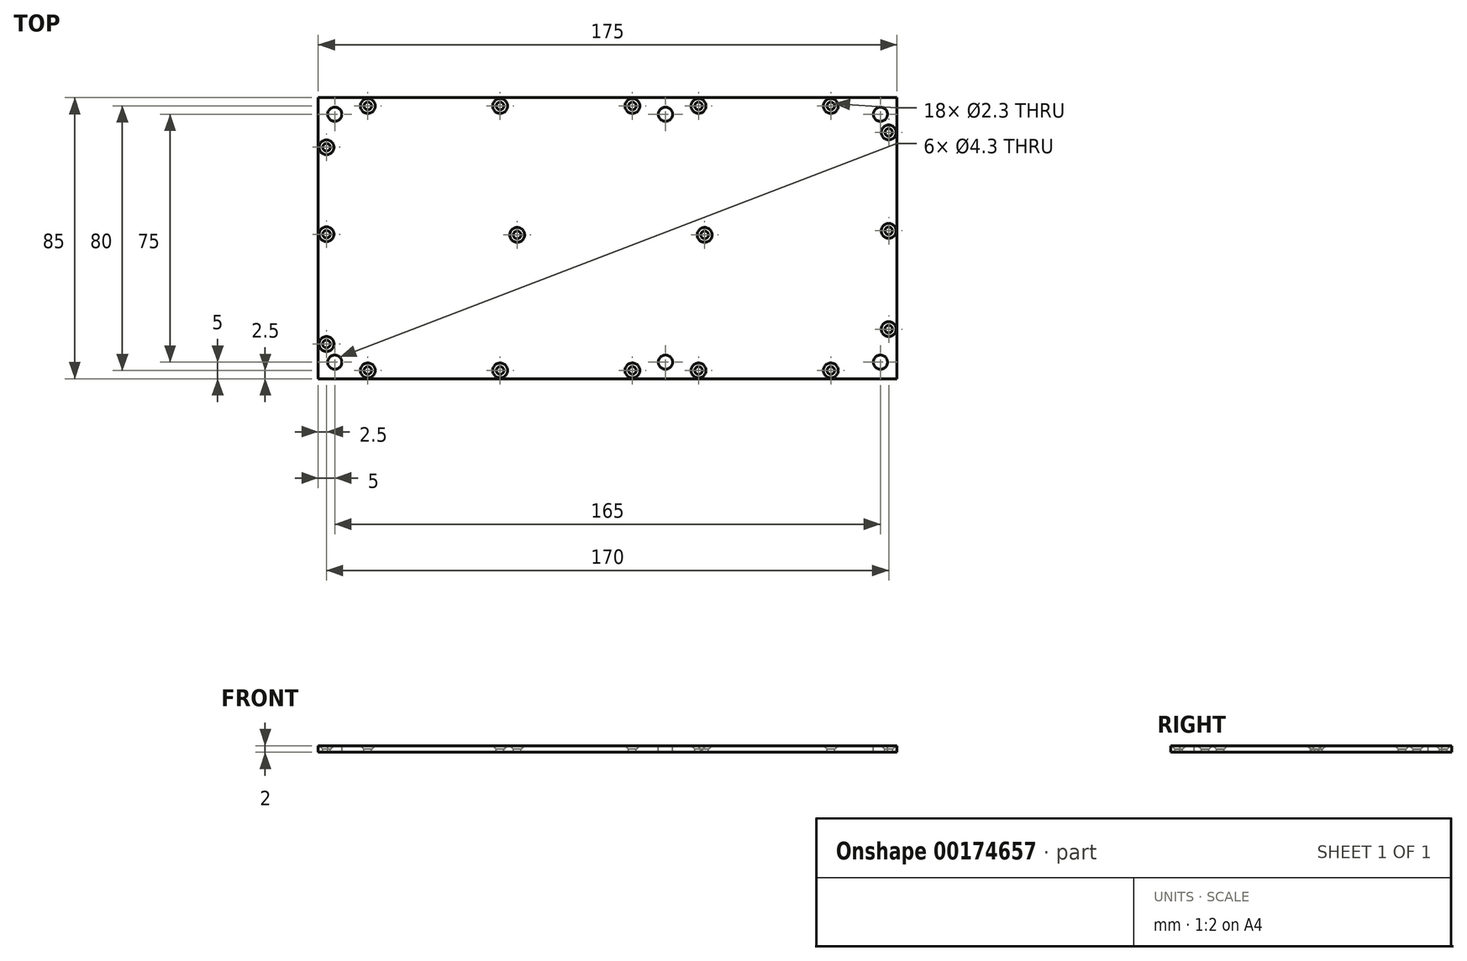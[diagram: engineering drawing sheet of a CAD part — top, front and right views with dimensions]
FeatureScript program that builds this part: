
annotation { "Feature Type Name" : "Feature", "Feature Type Description" : "" }
export const myFeature = defineFeature(function(context is Context, id is Id, definition is map)
    precondition{}
    {
        {
            var Q0;
            Q0=qCreatedBy(makeId("Top.planeOp"),FACE);
            var sketch = newSketch(context, id + "F0", { "sketchPlane" : qUnion([Q0])});
            skLineSegment(sketch, "E0", {"start": v(-87.5, 42.5) * mm, "end": v(87.5, 42.5) * mm});
            skLineSegment(sketch, "E1", {"start": v(87.5, 42.5) * mm, "end": v(87.5, -42.5) * mm});
            skLineSegment(sketch, "E2", {"start": v(87.5, -42.5) * mm, "end": v(-87.5, -42.5) * mm});
            skLineSegment(sketch, "E3", {"start": v(-87.5, -42.5) * mm, "end": v(-87.5, 42.5) * mm});
            skArc(sketch, "E4", {"start": v(-84.5, 37.5) * mm, "mid": v(-82.5, 35.5) * mm, "end": v(-80.5, 37.5) * mm});
            skArc(sketch, "E5", {"start": v(-80.5, 37.5) * mm, "mid": v(-82.5, 39.5) * mm, "end": v(-84.5, 37.5) * mm});
            skArc(sketch, "E6", {"start": v(15.5, 37.5) * mm, "mid": v(17.5, 35.5) * mm, "end": v(19.5, 37.5) * mm});
            skArc(sketch, "E7", {"start": v(19.5, 37.5) * mm, "mid": v(17.5, 39.5) * mm, "end": v(15.5, 37.5) * mm});
            skArc(sketch, "E8", {"start": v(80.5, 37.5) * mm, "mid": v(82.5, 35.5) * mm, "end": v(84.5, 37.5) * mm});
            skArc(sketch, "E9", {"start": v(84.5, 37.5) * mm, "mid": v(82.5, 39.5) * mm, "end": v(80.5, 37.5) * mm});
            skArc(sketch, "E10", {"start": v(80.5, -37.5) * mm, "mid": v(82.5, -39.5) * mm, "end": v(84.5, -37.5) * mm});
            skArc(sketch, "E11", {"start": v(84.5, -37.5) * mm, "mid": v(82.5, -35.5) * mm, "end": v(80.5, -37.5) * mm});
            skArc(sketch, "E12", {"start": v(15.5, -37.5) * mm, "mid": v(17.5, -39.5) * mm, "end": v(19.5, -37.5) * mm});
            skArc(sketch, "E13", {"start": v(19.5, -37.5) * mm, "mid": v(17.5, -35.5) * mm, "end": v(15.5, -37.5) * mm});
            skArc(sketch, "E14", {"start": v(-84.5, -37.5) * mm, "mid": v(-82.5, -39.5) * mm, "end": v(-80.5, -37.5) * mm});
            skArc(sketch, "E15", {"start": v(-80.5, -37.5) * mm, "mid": v(-82.5, -35.5) * mm, "end": v(-84.5, -37.5) * mm});
            skCircle(sketch, "E16", {"center": v(-72.5, 40) * mm, "radius": 1.15 * mm});
            skCircle(sketch, "E17", {"center": v(-72.5, 40) * mm, "radius": 2.25 * mm});
            skCircle(sketch, "E18", {"center": v(7.5, -40) * mm, "radius": 1.15 * mm});
            skCircle(sketch, "E19", {"center": v(7.5, -40) * mm, "radius": 2.25 * mm});
            skCircle(sketch, "E20", {"center": v(-32.5, -40) * mm, "radius": 1.15 * mm});
            skCircle(sketch, "E21", {"center": v(-32.5, -40) * mm, "radius": 2.25 * mm});
            skCircle(sketch, "E22", {"center": v(-72.5, -40) * mm, "radius": 1.15 * mm});
            skCircle(sketch, "E23", {"center": v(-72.5, -40) * mm, "radius": 2.25 * mm});
            skCircle(sketch, "E24", {"center": v(-85, -32) * mm, "radius": 1.15 * mm});
            skCircle(sketch, "E25", {"center": v(-85, -32) * mm, "radius": 2.25 * mm});
            skCircle(sketch, "E26", {"center": v(-85, 0) * mm, "radius": 1.15 * mm});
            skCircle(sketch, "E27", {"center": v(-85, 0) * mm, "radius": 2.25 * mm});
            skCircle(sketch, "E28", {"center": v(-85, 27.5) * mm, "radius": 1.15 * mm});
            skCircle(sketch, "E29", {"center": v(-85, 27.5) * mm, "radius": 2.25 * mm});
            skCircle(sketch, "E30", {"center": v(-32.5, 40) * mm, "radius": 1.15 * mm});
            skCircle(sketch, "E31", {"center": v(-32.5, 40) * mm, "radius": 2.25 * mm});
            skCircle(sketch, "E32", {"center": v(7.5, 40) * mm, "radius": 1.15 * mm});
            skCircle(sketch, "E33", {"center": v(7.5, 40) * mm, "radius": 2.25 * mm});
            skCircle(sketch, "E34", {"center": v(27.5, 40) * mm, "radius": 1.15 * mm});
            skCircle(sketch, "E35", {"center": v(27.5, 40) * mm, "radius": 2.25 * mm});
            skCircle(sketch, "E36", {"center": v(67.5, 40) * mm, "radius": 1.15 * mm});
            skCircle(sketch, "E37", {"center": v(67.5, 40) * mm, "radius": 2.25 * mm});
            skCircle(sketch, "E38", {"center": v(67.5, -40) * mm, "radius": 1.15 * mm});
            skCircle(sketch, "E39", {"center": v(67.5, -40) * mm, "radius": 2.25 * mm});
            skCircle(sketch, "E40", {"center": v(27.5, -40) * mm, "radius": 1.15 * mm});
            skCircle(sketch, "E41", {"center": v(27.5, -40) * mm, "radius": 2.25 * mm});
            skCircle(sketch, "E42", {"center": v(85, 24.3) * mm, "radius": 1.15 * mm});
            skCircle(sketch, "E43", {"center": v(85, 24.3) * mm, "radius": 2.25 * mm});
            skCircle(sketch, "E44", {"center": v(85, 0) * mm, "radius": 1.15 * mm});
            skCircle(sketch, "E45", {"center": v(85, 0) * mm, "radius": 2.25 * mm});
            skCircle(sketch, "E46", {"center": v(85, -27.5) * mm, "radius": 1.15 * mm});
            skCircle(sketch, "E47", {"center": v(85, -27.5) * mm, "radius": 2.25 * mm});
            skSolve(sketch);
        }
        {
            var Q0;
            Q0=makeQuery(id+"F0.imprint","IMPRINT",FACE,{"disambiguationData":[TD([[makeQuery(id+"F0.imprint","IMPRINT",EDGE,{"derivedFrom":sQuery(id+"F0.wireOp",EDGE,"E28")}),1.0]])]});
            var Q1;
            Q1=makeQuery(id+"F0.imprint","IMPRINT",FACE,{"disambiguationData":[TD([[makeQuery(id+"F0.imprint","IMPRINT",EDGE,{"derivedFrom":sQuery(id+"F0.wireOp",EDGE,"E28")}),-1.0]])]});
            var Q2;
            Q2=makeQuery(id+"F0.imprint","IMPRINT",FACE,{"disambiguationData":[TD([[makeQuery(id+"F0.imprint","IMPRINT",EDGE,{"derivedFrom":sQuery(id+"F0.wireOp",EDGE,"E32")}),1.0]])]});
            var Q3;
            Q3=makeQuery(id+"F0.imprint","IMPRINT",FACE,{"disambiguationData":[TD([[makeQuery(id+"F0.imprint","IMPRINT",EDGE,{"derivedFrom":sQuery(id+"F0.wireOp",EDGE,"E20")}),1.0]])]});
            var Q4;
            Q4=makeQuery(id+"F0.imprint","IMPRINT",FACE,{"disambiguationData":[TD([[makeQuery(id+"F0.imprint","IMPRINT",EDGE,{"derivedFrom":sQuery(id+"F0.wireOp",EDGE,"E18")}),1.0]])]});
            var Q5;
            Q5=makeQuery(id+"F0.imprint","IMPRINT",FACE,{"disambiguationData":[TD([[makeQuery(id+"F0.imprint","IMPRINT",EDGE,{"derivedFrom":sQuery(id+"F0.wireOp",EDGE,"E26")}),1.0]])]});
            var Q6;
            Q6=makeQuery(id+"F0.imprint","IMPRINT",FACE,{"disambiguationData":[TD([[makeQuery(id+"F0.imprint","IMPRINT",EDGE,{"derivedFrom":sQuery(id+"F0.wireOp",EDGE,"E30")}),1.0]])]});
            var Q7;
            Q7=makeQuery(id+"F0.imprint","IMPRINT",FACE,{"disambiguationData":[TD([[makeQuery(id+"F0.imprint","IMPRINT",EDGE,{"derivedFrom":sQuery(id+"F0.wireOp",EDGE,"E44")}),1.0]])]});
            var Q8;
            Q8=makeQuery(id+"F0.imprint","IMPRINT",FACE,{"disambiguationData":[TD([[makeQuery(id+"F0.imprint","IMPRINT",EDGE,{"derivedFrom":sQuery(id+"F0.wireOp",EDGE,"E16")}),1.0]])]});
            var Q9;
            Q9=makeQuery(id+"F0.imprint","IMPRINT",FACE,{"disambiguationData":[TD([[makeQuery(id+"F0.imprint","IMPRINT",EDGE,{"derivedFrom":sQuery(id+"F0.wireOp",EDGE,"E24")}),1.0]])]});
            var Q10;
            Q10=makeQuery(id+"F0.imprint","IMPRINT",FACE,{"disambiguationData":[TD([[makeQuery(id+"F0.imprint","IMPRINT",EDGE,{"derivedFrom":sQuery(id+"F0.wireOp",EDGE,"E22")}),1.0]])]});
            var Q11;
            Q11=makeQuery(id+"F0.imprint","IMPRINT",FACE,{"disambiguationData":[TD([[makeQuery(id+"F0.imprint","IMPRINT",EDGE,{"derivedFrom":sQuery(id+"F0.wireOp",EDGE,"E34")}),1.0]])]});
            var Q12;
            Q12=makeQuery(id+"F0.imprint","IMPRINT",FACE,{"disambiguationData":[TD([[makeQuery(id+"F0.imprint","IMPRINT",EDGE,{"derivedFrom":sQuery(id+"F0.wireOp",EDGE,"E40")}),1.0]])]});
            var Q13;
            Q13=makeQuery(id+"F0.imprint","IMPRINT",FACE,{"disambiguationData":[TD([[makeQuery(id+"F0.imprint","IMPRINT",EDGE,{"derivedFrom":sQuery(id+"F0.wireOp",EDGE,"E14")}),1.0]])]});
            var Q14;
            Q14=makeQuery(id+"F0.imprint","IMPRINT",FACE,{"disambiguationData":[TD([[makeQuery(id+"F0.imprint","IMPRINT",EDGE,{"derivedFrom":sQuery(id+"F0.wireOp",EDGE,"E12")}),1.0]])]});
            var Q15;
            Q15=makeQuery(id+"F0.imprint","IMPRINT",FACE,{"disambiguationData":[TD([[makeQuery(id+"F0.imprint","IMPRINT",EDGE,{"derivedFrom":sQuery(id+"F0.wireOp",EDGE,"E8")}),1.0]])]});
            var Q16;
            Q16=makeQuery(id+"F0.imprint","IMPRINT",FACE,{"disambiguationData":[TD([[makeQuery(id+"F0.imprint","IMPRINT",EDGE,{"derivedFrom":sQuery(id+"F0.wireOp",EDGE,"E6")}),1.0]])]});
            var Q17;
            Q17=makeQuery(id+"F0.imprint","IMPRINT",FACE,{"disambiguationData":[TD([[makeQuery(id+"F0.imprint","IMPRINT",EDGE,{"derivedFrom":sQuery(id+"F0.wireOp",EDGE,"E4")}),1.0]])]});
            var Q18;
            Q18=makeQuery(id+"F0.imprint","IMPRINT",FACE,{"disambiguationData":[TD([[makeQuery(id+"F0.imprint","IMPRINT",EDGE,{"derivedFrom":sQuery(id+"F0.wireOp",EDGE,"E36")}),1.0]])]});
            var Q19;
            Q19=makeQuery(id+"F0.imprint","IMPRINT",FACE,{"disambiguationData":[TD([[makeQuery(id+"F0.imprint","IMPRINT",EDGE,{"derivedFrom":sQuery(id+"F0.wireOp",EDGE,"E42")}),1.0]])]});
            var Q20;
            Q20=makeQuery(id+"F0.imprint","IMPRINT",FACE,{"disambiguationData":[TD([[makeQuery(id+"F0.imprint","IMPRINT",EDGE,{"derivedFrom":sQuery(id+"F0.wireOp",EDGE,"E42")}),-1.0]])]});
            var Q21;
            Q21=makeQuery(id+"F0.imprint","IMPRINT",FACE,{"disambiguationData":[TD([[makeQuery(id+"F0.imprint","IMPRINT",EDGE,{"derivedFrom":sQuery(id+"F0.wireOp",EDGE,"E24")}),-1.0]])]});
            var Q22;
            Q22=makeQuery(id+"F0.imprint","IMPRINT",FACE,{"disambiguationData":[TD([[makeQuery(id+"F0.imprint","IMPRINT",EDGE,{"derivedFrom":sQuery(id+"F0.wireOp",EDGE,"E22")}),-1.0]])]});
            var Q23;
            Q23=makeQuery(id+"F0.imprint","IMPRINT",FACE,{"disambiguationData":[TD([[makeQuery(id+"F0.imprint","IMPRINT",EDGE,{"derivedFrom":sQuery(id+"F0.wireOp",EDGE,"E20")}),-1.0]])]});
            var Q24;
            Q24=makeQuery(id+"F0.imprint","IMPRINT",FACE,{"disambiguationData":[TD([[makeQuery(id+"F0.imprint","IMPRINT",EDGE,{"derivedFrom":sQuery(id+"F0.wireOp",EDGE,"E18")}),-1.0]])]});
            var Q25;
            Q25=makeQuery(id+"F0.imprint","IMPRINT",FACE,{"disambiguationData":[TD([[makeQuery(id+"F0.imprint","IMPRINT",EDGE,{"derivedFrom":sQuery(id+"F0.wireOp",EDGE,"E16")}),-1.0]])]});
            var Q26;
            Q26=makeQuery(id+"F0.imprint","IMPRINT",FACE,{"disambiguationData":[TD([[makeQuery(id+"F0.imprint","IMPRINT",EDGE,{"derivedFrom":sQuery(id+"F0.wireOp",EDGE,"E32")}),-1.0]])]});
            var Q27;
            Q27=makeQuery(id+"F0.imprint","IMPRINT",FACE,{"disambiguationData":[TD([[makeQuery(id+"F0.imprint","IMPRINT",EDGE,{"derivedFrom":sQuery(id+"F0.wireOp",EDGE,"E30")}),-1.0]])]});
            var Q28;
            Q28=makeQuery(id+"F0.imprint","IMPRINT",FACE,{"disambiguationData":[TD([[makeQuery(id+"F0.imprint","IMPRINT",EDGE,{"derivedFrom":sQuery(id+"F0.wireOp",EDGE,"E44")}),-1.0]])]});
            var Q29;
            Q29=makeQuery(id+"F0.imprint","IMPRINT",FACE,{"disambiguationData":[TD([[makeQuery(id+"F0.imprint","IMPRINT",EDGE,{"derivedFrom":sQuery(id+"F0.wireOp",EDGE,"E40")}),-1.0]])]});
            var Q30;
            Q30=makeQuery(id+"F0.imprint","IMPRINT",FACE,{"disambiguationData":[TD([[makeQuery(id+"F0.imprint","IMPRINT",EDGE,{"derivedFrom":sQuery(id+"F0.wireOp",EDGE,"E26")}),-1.0]])]});
            var Q31;
            Q31=makeQuery(id+"F0.imprint","IMPRINT",FACE,{"disambiguationData":[TD([[makeQuery(id+"F0.imprint","IMPRINT",EDGE,{"derivedFrom":sQuery(id+"F0.wireOp",EDGE,"E36")}),-1.0]])]});
            var Q32;
            Q32=makeQuery(id+"F0.imprint","IMPRINT",FACE,{"disambiguationData":[TD([[makeQuery(id+"F0.imprint","IMPRINT",EDGE,{"derivedFrom":sQuery(id+"F0.wireOp",EDGE,"E34")}),-1.0]])]});
            var Q33;
            Q33=makeQuery(id+"F0.imprint","IMPRINT",FACE,{"disambiguationData":[TD([[makeQuery(id+"F0.imprint","IMPRINT",EDGE,{"derivedFrom":sQuery(id+"F0.wireOp",EDGE,"E3")}),-1.0]])]});
            var Q34;
            Q34=makeQuery(id+"F0.imprint","IMPRINT",FACE,{"disambiguationData":[TD([[makeQuery(id+"F0.imprint","IMPRINT",EDGE,{"derivedFrom":sQuery(id+"F0.wireOp",EDGE,"E38")}),1.0]])]});
            var Q35;
            Q35=makeQuery(id+"F0.imprint","IMPRINT",FACE,{"disambiguationData":[TD([[makeQuery(id+"F0.imprint","IMPRINT",EDGE,{"derivedFrom":sQuery(id+"F0.wireOp",EDGE,"E46")}),1.0]])]});
            var Q36;
            Q36=makeQuery(id+"F0.imprint","IMPRINT",FACE,{"disambiguationData":[TD([[makeQuery(id+"F0.imprint","IMPRINT",EDGE,{"derivedFrom":sQuery(id+"F0.wireOp",EDGE,"E10")}),1.0]])]});
            var Q37;
            Q37=makeQuery(id+"F0.imprint","IMPRINT",FACE,{"disambiguationData":[TD([[makeQuery(id+"F0.imprint","IMPRINT",EDGE,{"derivedFrom":sQuery(id+"F0.wireOp",EDGE,"E38")}),-1.0]])]});
            var Q38;
            Q38=makeQuery(id+"F0.imprint","IMPRINT",FACE,{"disambiguationData":[TD([[makeQuery(id+"F0.imprint","IMPRINT",EDGE,{"derivedFrom":sQuery(id+"F0.wireOp",EDGE,"E46")}),-1.0]])]});
            extrude(context, id + "F1", {"entities" : qUnion([Q0, Q1, Q2, Q3, Q4, Q5, Q6, Q7, Q8, Q9, Q10, Q11, Q12, Q13, Q14, Q15, Q16, Q17, Q18, Q19, Q20, Q21, Q22, Q23, Q24, Q25, Q26, Q27, Q28, Q29, Q30, Q31, Q32, Q33, Q34, Q35, Q36, Q37, Q38]), "oppositeDirection" : true, "depth" : 2 * mm});
        }
        {
            var Q0;
            Q0=sQuery(id+"F0.wireOp",VERTEX,"E4.center");
            var Q1;
            Q1=sQuery(id+"F0.wireOp",VERTEX,"E6.center");
            var Q2;
            Q2=sQuery(id+"F0.wireOp",VERTEX,"E8.center");
            var Q3;
            Q3=sQuery(id+"F0.wireOp",VERTEX,"E10.center");
            var Q4;
            Q4=sQuery(id+"F0.wireOp",VERTEX,"E14.center");
            var Q5;
            Q5=sQuery(id+"F0.wireOp",VERTEX,"E12.center");
            var Q6;
            Q6=makeQuery(id+"F1.opExtrude","SWEPT_BODY",BODY,{"disambiguationData":[OSD([sQuery(id+"F0.wireOp",EDGE,"E3"),sQuery(id+"F0.wireOp",EDGE,"E0"),sQuery(id+"F0.wireOp",EDGE,"E1"),sQuery(id+"F0.wireOp",EDGE,"E2")])]});
            hole(context, id + "F2", {"style" : HoleStyle.SIMPLE, "endStyle" : HoleEndStyle.THROUGH, "holeDiameter" : 4.3 * mm, "startFromSketch" : true, "locations" : qUnion([Q0, Q1, Q2, Q3, Q4, Q5]), "scope" : qUnion([Q6]), "isTappedThrough" : true});
        }
        {
            var Q0;
            Q0=makeQuery(id+"F1.opExtrude","CAP_FACE",FACE,{"disambiguationData":[OSD([sQuery(id+"F0.wireOp",EDGE,"E3"),sQuery(id+"F0.wireOp",EDGE,"E0"),sQuery(id+"F0.wireOp",EDGE,"E1"),sQuery(id+"F0.wireOp",EDGE,"E2")])],"isStart":true});
            var sketch = newSketch(context, id + "F3", { "sketchPlane" : qUnion([Q0])});
            skArc(sketch, "E48", {"start": v(47.04, 28.5) * mm, "mid": v(46.24, 29.3) * mm, "end": v(45.44, 28.5) * mm});
            skArc(sketch, "E49", {"start": v(45.44, 28.5) * mm, "mid": v(46.24, 27.7) * mm, "end": v(47.04, 28.5) * mm});
            skArc(sketch, "E50", {"start": v(61.54, 28.5) * mm, "mid": v(60.74, 29.3) * mm, "end": v(59.94, 28.5) * mm});
            skArc(sketch, "E51", {"start": v(59.94, 28.5) * mm, "mid": v(60.74, 27.7) * mm, "end": v(61.54, 28.5) * mm});
            skArc(sketch, "E52", {"start": v(61.54, 14) * mm, "mid": v(60.74, 14.8) * mm, "end": v(59.94, 14) * mm});
            skArc(sketch, "E53", {"start": v(59.94, 14) * mm, "mid": v(60.74, 13.2) * mm, "end": v(61.54, 14) * mm});
            skArc(sketch, "E54", {"start": v(47.04, 14) * mm, "mid": v(46.24, 14.8) * mm, "end": v(45.44, 14) * mm});
            skArc(sketch, "E55", {"start": v(45.44, 14) * mm, "mid": v(46.24, 13.2) * mm, "end": v(47.04, 14) * mm});
            skLineSegment(sketch, "E56", {"start": v(62.6, 6.55) * mm, "end": v(44.4, 6.55) * mm});
            skArc(sketch, "E57", {"start": v(44.4, 6.55) * mm, "mid": v(44.04, 6.7) * mm, "end": v(43.9, 7.05) * mm});
            skLineSegment(sketch, "E58", {"start": v(43.9, 7.05) * mm, "end": v(43.9, 30.45) * mm});
            skArc(sketch, "E59", {"start": v(43.9, 30.45) * mm, "mid": v(44.04, 30.8) * mm, "end": v(44.4, 30.95) * mm});
            skLineSegment(sketch, "E60", {"start": v(44.4, 30.95) * mm, "end": v(62.6, 30.95) * mm});
            skArc(sketch, "E61", {"start": v(62.6, 30.95) * mm, "mid": v(62.94, 30.8) * mm, "end": v(63.1, 30.45) * mm});
            skLineSegment(sketch, "E62", {"start": v(63.1, 30.45) * mm, "end": v(63.1, 7.05) * mm});
            skArc(sketch, "E63", {"start": v(63.1, 7.05) * mm, "mid": v(62.94, 6.7) * mm, "end": v(62.6, 6.55) * mm});
            skArc(sketch, "E64", {"start": v(-9.64, 12.56) * mm, "mid": v(-9.5, 12.2) * mm, "end": v(-9.14, 12.06) * mm});
            skLineSegment(sketch, "E65", {"start": v(-9.14, 12.06) * mm, "end": v(-0.1, 12.06) * mm});
            skArc(sketch, "E66", {"start": v(-0.1, 12.06) * mm, "mid": v(0.25, 12.2) * mm, "end": v(0.4, 12.56) * mm});
            skLineSegment(sketch, "E67", {"start": v(0.4, 12.56) * mm, "end": v(0.4, 17.16) * mm});
            skArc(sketch, "E68", {"start": v(0.4, 17.16) * mm, "mid": v(0.25, 17.5) * mm, "end": v(-0.1, 17.65) * mm});
            skLineSegment(sketch, "E69", {"start": v(-0.1, 17.65) * mm, "end": v(-0.1, 31.13) * mm});
            skArc(sketch, "E70", {"start": v(-0.1, 31.13) * mm, "mid": v(0.25, 31.27) * mm, "end": v(0.4, 31.62) * mm});
            skLineSegment(sketch, "E71", {"start": v(0.4, 31.62) * mm, "end": v(0.4, 36.22) * mm});
            skArc(sketch, "E72", {"start": v(0.4, 36.22) * mm, "mid": v(0.25, 36.58) * mm, "end": v(-0.1, 36.72) * mm});
            skLineSegment(sketch, "E73", {"start": v(-0.1, 36.72) * mm, "end": v(-9.14, 36.72) * mm});
            skArc(sketch, "E74", {"start": v(-9.14, 36.72) * mm, "mid": v(-9.5, 36.58) * mm, "end": v(-9.64, 36.22) * mm});
            skLineSegment(sketch, "E75", {"start": v(-9.64, 36.22) * mm, "end": v(-9.64, 31.62) * mm});
            skArc(sketch, "E76", {"start": v(-9.64, 31.62) * mm, "mid": v(-9.5, 31.27) * mm, "end": v(-9.14, 31.13) * mm});
            skLineSegment(sketch, "E77", {"start": v(-9.14, 31.13) * mm, "end": v(-9.14, 17.65) * mm});
            skArc(sketch, "E78", {"start": v(-9.14, 17.65) * mm, "mid": v(-9.5, 17.5) * mm, "end": v(-9.64, 17.16) * mm});
            skLineSegment(sketch, "E79", {"start": v(-9.64, 17.16) * mm, "end": v(-9.64, 12.56) * mm});
            skLineSegment(sketch, "E80", {"start": v(76.69, 23.8) * mm, "end": v(76.69, 24.8) * mm});
            skLineSegment(sketch, "E81", {"start": v(76.69, 24.8) * mm, "end": v(82.19, 24.8) * mm});
            skLineSegment(sketch, "E82", {"start": v(82.19, 24.8) * mm, "end": v(82.19, 23.8) * mm});
            skLineSegment(sketch, "E83", {"start": v(82.19, 23.8) * mm, "end": v(76.69, 23.8) * mm});
            skLineSegment(sketch, "E84", {"start": v(82.2, 23.66) * mm, "end": v(82.2, 24.94) * mm});
            skLineSegment(sketch, "E85", {"start": v(82.2, 24.94) * mm, "end": v(79.3, 24.94) * mm});
            skLineSegment(sketch, "E86", {"start": v(79.3, 24.94) * mm, "end": v(79.3, 23.66) * mm});
            skLineSegment(sketch, "E87", {"start": v(79.3, 23.66) * mm, "end": v(82.2, 23.66) * mm});
            skArc(sketch, "E88", {"start": v(61.34, 28.5) * mm, "mid": v(60.74, 29.1) * mm, "end": v(60.14, 28.5) * mm});
            skArc(sketch, "E89", {"start": v(60.14, 28.5) * mm, "mid": v(60.74, 27.9) * mm, "end": v(61.34, 28.5) * mm});
            skArc(sketch, "E90", {"start": v(-83.5, -25.16) * mm, "mid": v(-83.24, -26.74) * mm, "end": v(-82.5, -28.16) * mm});
            skLineSegment(sketch, "E91", {"start": v(-82.5, -29.94) * mm, "end": v(-82.5, -28.16) * mm});
            skArc(sketch, "E92", {"start": v(-3.6, 14.1) * mm, "mid": v(-4.62, 15.13) * mm, "end": v(-5.64, 14.1) * mm});
            skArc(sketch, "E93", {"start": v(-5.64, 14.1) * mm, "mid": v(-4.62, 13.08) * mm, "end": v(-3.6, 14.1) * mm});
            skArc(sketch, "E94", {"start": v(-3.6, 34.68) * mm, "mid": v(-4.62, 35.7) * mm, "end": v(-5.65, 34.68) * mm});
            skArc(sketch, "E95", {"start": v(-5.65, 34.68) * mm, "mid": v(-4.62, 33.65) * mm, "end": v(-3.6, 34.68) * mm});
            skArc(sketch, "E96", {"start": v(30.15, 1) * mm, "mid": v(29.35, 1.8) * mm, "end": v(28.55, 1) * mm});
            skArc(sketch, "E97", {"start": v(28.55, 1) * mm, "mid": v(29.35, 0.2) * mm, "end": v(30.15, 1) * mm});
            skArc(sketch, "E98", {"start": v(43.3, 1) * mm, "mid": v(42.5, 1.8) * mm, "end": v(41.7, 1) * mm});
            skArc(sketch, "E99", {"start": v(41.7, 1) * mm, "mid": v(42.5, 0.2) * mm, "end": v(43.3, 1) * mm});
            skArc(sketch, "E100", {"start": v(79.3, -24.5) * mm, "mid": v(78.5, -23.7) * mm, "end": v(77.7, -24.5) * mm});
            skArc(sketch, "E101", {"start": v(77.7, -24.5) * mm, "mid": v(78.5, -25.3) * mm, "end": v(79.3, -24.5) * mm});
            skArc(sketch, "E102", {"start": v(57.41, -12.94) * mm, "mid": v(56.61, -12.14) * mm, "end": v(55.81, -12.94) * mm});
            skArc(sketch, "E103", {"start": v(55.81, -12.94) * mm, "mid": v(56.61, -13.74) * mm, "end": v(57.41, -12.94) * mm});
            skArc(sketch, "E104", {"start": v(67.3, -33.5) * mm, "mid": v(66.5, -32.7) * mm, "end": v(65.7, -33.5) * mm});
            skArc(sketch, "E105", {"start": v(65.7, -33.5) * mm, "mid": v(66.5, -34.3) * mm, "end": v(67.3, -33.5) * mm});
            skArc(sketch, "E106", {"start": v(28.3, -34.5) * mm, "mid": v(27.5, -33.7) * mm, "end": v(26.7, -34.5) * mm});
            skArc(sketch, "E107", {"start": v(26.7, -34.5) * mm, "mid": v(27.5, -35.3) * mm, "end": v(28.3, -34.5) * mm});
            skArc(sketch, "E108", {"start": v(4.3, -34.5) * mm, "mid": v(3.5, -33.7) * mm, "end": v(2.7, -34.5) * mm});
            skArc(sketch, "E109", {"start": v(2.7, -34.5) * mm, "mid": v(3.5, -35.3) * mm, "end": v(4.3, -34.5) * mm});
            skArc(sketch, "E110", {"start": v(-11.7, -34.4) * mm, "mid": v(-12.5, -33.6) * mm, "end": v(-13.3, -34.4) * mm});
            skArc(sketch, "E111", {"start": v(-13.3, -34.4) * mm, "mid": v(-12.5, -35.2) * mm, "end": v(-11.7, -34.4) * mm});
            skArc(sketch, "E112", {"start": v(-37.7, -34.5) * mm, "mid": v(-38.5, -33.7) * mm, "end": v(-39.3, -34.5) * mm});
            skArc(sketch, "E113", {"start": v(-39.3, -34.5) * mm, "mid": v(-38.5, -35.3) * mm, "end": v(-37.7, -34.5) * mm});
            skArc(sketch, "E114", {"start": v(-69.7, -34.5) * mm, "mid": v(-70.5, -33.7) * mm, "end": v(-71.3, -34.5) * mm});
            skArc(sketch, "E115", {"start": v(-71.3, -34.5) * mm, "mid": v(-70.5, -35.3) * mm, "end": v(-69.7, -34.5) * mm});
            skArc(sketch, "E116", {"start": v(40.08, 32.1) * mm, "mid": v(39.28, 32.9) * mm, "end": v(38.48, 32.1) * mm});
            skArc(sketch, "E117", {"start": v(38.48, 32.1) * mm, "mid": v(39.28, 31.3) * mm, "end": v(40.08, 32.1) * mm});
            skArc(sketch, "E118", {"start": v(41.3, 18.5) * mm, "mid": v(40.5, 19.3) * mm, "end": v(39.7, 18.5) * mm});
            skArc(sketch, "E119", {"start": v(39.7, 18.5) * mm, "mid": v(40.5, 17.7) * mm, "end": v(41.3, 18.5) * mm});
            skArc(sketch, "E120", {"start": v(21.81, 29.5) * mm, "mid": v(21.01, 30.3) * mm, "end": v(20.21, 29.5) * mm});
            skArc(sketch, "E121", {"start": v(20.21, 29.5) * mm, "mid": v(21.01, 28.7) * mm, "end": v(21.81, 29.5) * mm});
            skArc(sketch, "E122", {"start": v(4.44, 35.03) * mm, "mid": v(3.64, 35.83) * mm, "end": v(2.84, 35.03) * mm});
            skArc(sketch, "E123", {"start": v(2.84, 35.03) * mm, "mid": v(3.64, 34.23) * mm, "end": v(4.44, 35.03) * mm});
            skArc(sketch, "E124", {"start": v(12.58, 19.26) * mm, "mid": v(11.78, 20.06) * mm, "end": v(10.98, 19.26) * mm});
            skArc(sketch, "E125", {"start": v(10.98, 19.26) * mm, "mid": v(11.78, 18.46) * mm, "end": v(12.58, 19.26) * mm});
            skArc(sketch, "E126", {"start": v(13.3, 1) * mm, "mid": v(12.5, 1.8) * mm, "end": v(11.7, 1) * mm});
            skArc(sketch, "E127", {"start": v(11.7, 1) * mm, "mid": v(12.5, 0.2) * mm, "end": v(13.3, 1) * mm});
            skArc(sketch, "E128", {"start": v(-16.7, 1) * mm, "mid": v(-17.5, 1.8) * mm, "end": v(-18.3, 1) * mm});
            skArc(sketch, "E129", {"start": v(-18.3, 1) * mm, "mid": v(-17.5, 0.2) * mm, "end": v(-16.7, 1) * mm});
            skArc(sketch, "E130", {"start": v(-11.48, 14.2) * mm, "mid": v(-12.28, 15) * mm, "end": v(-13.08, 14.2) * mm});
            skArc(sketch, "E131", {"start": v(-13.08, 14.2) * mm, "mid": v(-12.28, 13.4) * mm, "end": v(-11.48, 14.2) * mm});
            skArc(sketch, "E132", {"start": v(-13.7, 34.4) * mm, "mid": v(-14.5, 35.2) * mm, "end": v(-15.3, 34.4) * mm});
            skArc(sketch, "E133", {"start": v(-15.3, 34.4) * mm, "mid": v(-14.5, 33.6) * mm, "end": v(-13.7, 34.4) * mm});
            skArc(sketch, "E134", {"start": v(-46.7, 1) * mm, "mid": v(-47.5, 1.8) * mm, "end": v(-48.3, 1) * mm});
            skArc(sketch, "E135", {"start": v(-48.3, 1) * mm, "mid": v(-47.5, 0.2) * mm, "end": v(-46.7, 1) * mm});
            skArc(sketch, "E136", {"start": v(-29.75, 20.38) * mm, "mid": v(-30.55, 21.18) * mm, "end": v(-31.35, 20.38) * mm});
            skArc(sketch, "E137", {"start": v(-31.35, 20.38) * mm, "mid": v(-30.55, 19.58) * mm, "end": v(-29.75, 20.38) * mm});
            skArc(sketch, "E138", {"start": v(-34.7, 34.4) * mm, "mid": v(-35.5, 35.2) * mm, "end": v(-36.3, 34.4) * mm});
            skArc(sketch, "E139", {"start": v(-36.3, 34.4) * mm, "mid": v(-35.5, 33.6) * mm, "end": v(-34.7, 34.4) * mm});
            skArc(sketch, "E140", {"start": v(-65.05, 34.3) * mm, "mid": v(-65.85, 35.1) * mm, "end": v(-66.65, 34.3) * mm});
            skArc(sketch, "E141", {"start": v(-66.65, 34.3) * mm, "mid": v(-65.85, 33.5) * mm, "end": v(-65.05, 34.3) * mm});
            skArc(sketch, "E142", {"start": v(-66.7, 19.5) * mm, "mid": v(-67.5, 20.3) * mm, "end": v(-68.3, 19.5) * mm});
            skArc(sketch, "E143", {"start": v(-68.3, 19.5) * mm, "mid": v(-67.5, 18.7) * mm, "end": v(-66.7, 19.5) * mm});
            skArc(sketch, "E144", {"start": v(-26.55, 1) * mm, "mid": v(-27.35, 1.8) * mm, "end": v(-28.15, 1) * mm});
            skArc(sketch, "E145", {"start": v(-28.15, 1) * mm, "mid": v(-27.35, 0.2) * mm, "end": v(-26.55, 1) * mm});
            skArc(sketch, "E146", {"start": v(-78.58, 14.5) * mm, "mid": v(-79.38, 15.3) * mm, "end": v(-80.18, 14.5) * mm});
            skArc(sketch, "E147", {"start": v(-80.18, 14.5) * mm, "mid": v(-79.38, 13.7) * mm, "end": v(-78.58, 14.5) * mm});
            skArc(sketch, "E148", {"start": v(-46.87, 35.58) * mm, "mid": v(-48.37, 37.08) * mm, "end": v(-49.87, 35.58) * mm});
            skArc(sketch, "E149", {"start": v(-49.87, 35.58) * mm, "mid": v(-48.37, 34.08) * mm, "end": v(-46.87, 35.58) * mm});
            skArc(sketch, "E150", {"start": v(-69.63, 35.58) * mm, "mid": v(-71.13, 37.08) * mm, "end": v(-72.63, 35.58) * mm});
            skArc(sketch, "E151", {"start": v(-72.63, 35.58) * mm, "mid": v(-71.13, 34.08) * mm, "end": v(-69.63, 35.58) * mm});
            skArc(sketch, "E152", {"start": v(82.5, 27.94) * mm, "mid": v(82.12, 29.85) * mm, "end": v(81.04, 31.47) * mm});
            skLineSegment(sketch, "E153", {"start": v(82.5, 27.94) * mm, "end": v(82.5, -27.94) * mm});
            skLineSegment(sketch, "E154", {"start": v(8.95, -37.5) * mm, "end": v(-72.94, -37.5) * mm});
            skLineSegment(sketch, "E155", {"start": v(87.5, -42.5) * mm, "end": v(-87.5, -42.5) * mm});
            skArc(sketch, "E156", {"start": v(68.3, 40) * mm, "mid": v(67.5, 40.8) * mm, "end": v(66.7, 40) * mm});
            skArc(sketch, "E157", {"start": v(66.7, 40) * mm, "mid": v(67.5, 39.2) * mm, "end": v(68.3, 40) * mm});
            skArc(sketch, "E158", {"start": v(-82.5, -2.86) * mm, "mid": v(-83.24, -4.28) * mm, "end": v(-83.5, -5.86) * mm});
            skArc(sketch, "E159", {"start": v(85.8, 24.3) * mm, "mid": v(85, 25.1) * mm, "end": v(84.2, 24.3) * mm});
            skArc(sketch, "E160", {"start": v(84.2, 24.3) * mm, "mid": v(85, 23.5) * mm, "end": v(85.8, 24.3) * mm});
            skArc(sketch, "E161", {"start": v(-76.47, -36.04) * mm, "mid": v(-74.85, -37.12) * mm, "end": v(-72.94, -37.5) * mm});
            skLineSegment(sketch, "E162", {"start": v(-83.5, -5.86) * mm, "end": v(-83.5, -26.94) * mm});
            skArc(sketch, "E163", {"start": v(-83.5, -26.94) * mm, "mid": v(-83.12, -28.85) * mm, "end": v(-82.04, -30.47) * mm});
            skLineSegment(sketch, "E164", {"start": v(-87.5, -42.5) * mm, "end": v(-87.5, 42.5) * mm});
            skLineSegment(sketch, "E165", {"start": v(-76.47, 36.04) * mm, "end": v(-81.04, 31.47) * mm});
            skArc(sketch, "E166", {"start": v(-72.94, 37.5) * mm, "mid": v(-74.85, 37.12) * mm, "end": v(-76.47, 36.04) * mm});
            skLineSegment(sketch, "E167", {"start": v(-72.94, 37.5) * mm, "end": v(8.95, 37.5) * mm});
            skArc(sketch, "E168", {"start": v(12.49, 36.04) * mm, "mid": v(10.86, 37.12) * mm, "end": v(8.95, 37.5) * mm});
            skLineSegment(sketch, "E169", {"start": v(12.49, 36.04) * mm, "end": v(13.98, 34.54) * mm});
            skArc(sketch, "E170", {"start": v(13.98, 34.54) * mm, "mid": v(17.51, 33.08) * mm, "end": v(21.05, 34.54) * mm});
            skLineSegment(sketch, "E171", {"start": v(21.05, 34.54) * mm, "end": v(22.54, 36.04) * mm});
            skArc(sketch, "E172", {"start": v(26.08, 37.5) * mm, "mid": v(24.16, 37.12) * mm, "end": v(22.54, 36.04) * mm});
            skLineSegment(sketch, "E173", {"start": v(26.08, 37.5) * mm, "end": v(72.94, 37.5) * mm});
            skArc(sketch, "E174", {"start": v(76.47, 36.04) * mm, "mid": v(74.85, 37.12) * mm, "end": v(72.94, 37.5) * mm});
            skLineSegment(sketch, "E175", {"start": v(76.47, 36.04) * mm, "end": v(81.04, 31.47) * mm});
            skArc(sketch, "E176", {"start": v(81.04, -31.47) * mm, "mid": v(82.12, -29.85) * mm, "end": v(82.5, -27.94) * mm});
            skLineSegment(sketch, "E177", {"start": v(76.47, -36.04) * mm, "end": v(81.04, -31.47) * mm});
            skArc(sketch, "E178", {"start": v(72.94, -37.5) * mm, "mid": v(74.85, -37.12) * mm, "end": v(76.47, -36.04) * mm});
            skLineSegment(sketch, "E179", {"start": v(72.94, -37.5) * mm, "end": v(26.08, -37.5) * mm});
            skArc(sketch, "E180", {"start": v(22.54, -36.04) * mm, "mid": v(24.16, -37.12) * mm, "end": v(26.08, -37.5) * mm});
            skLineSegment(sketch, "E181", {"start": v(21.05, -34.54) * mm, "end": v(22.54, -36.04) * mm});
            skArc(sketch, "E182", {"start": v(21.05, -34.54) * mm, "mid": v(17.51, -33.08) * mm, "end": v(13.98, -34.54) * mm});
            skLineSegment(sketch, "E183", {"start": v(12.49, -36.04) * mm, "end": v(13.98, -34.54) * mm});
            skArc(sketch, "E184", {"start": v(8.95, -37.5) * mm, "mid": v(10.86, -37.12) * mm, "end": v(12.49, -36.04) * mm});
            skArc(sketch, "E185", {"start": v(68.3, -40) * mm, "mid": v(67.5, -39.2) * mm, "end": v(66.7, -40) * mm});
            skArc(sketch, "E186", {"start": v(66.7, -40) * mm, "mid": v(67.5, -40.8) * mm, "end": v(68.3, -40) * mm});
            skArc(sketch, "E187", {"start": v(85.8, -27.5) * mm, "mid": v(85, -26.7) * mm, "end": v(84.2, -27.5) * mm});
            skArc(sketch, "E188", {"start": v(84.2, -27.5) * mm, "mid": v(85, -28.3) * mm, "end": v(85.8, -27.5) * mm});
            skArc(sketch, "E189", {"start": v(85.8, 0) * mm, "mid": v(85, 0.8) * mm, "end": v(84.2, 0) * mm});
            skArc(sketch, "E190", {"start": v(84.2, 0) * mm, "mid": v(85, -0.8) * mm, "end": v(85.8, 0) * mm});
            skArc(sketch, "E191", {"start": v(28.3, -40) * mm, "mid": v(27.5, -39.2) * mm, "end": v(26.7, -40) * mm});
            skArc(sketch, "E192", {"start": v(26.7, -40) * mm, "mid": v(27.5, -40.8) * mm, "end": v(28.3, -40) * mm});
            skArc(sketch, "E193", {"start": v(8.3, -40) * mm, "mid": v(7.5, -39.2) * mm, "end": v(6.7, -40) * mm});
            skArc(sketch, "E194", {"start": v(6.7, -40) * mm, "mid": v(7.5, -40.8) * mm, "end": v(8.3, -40) * mm});
            skArc(sketch, "E195", {"start": v(-31.7, -40) * mm, "mid": v(-32.5, -39.2) * mm, "end": v(-33.3, -40) * mm});
            skArc(sketch, "E196", {"start": v(-33.3, -40) * mm, "mid": v(-32.5, -40.8) * mm, "end": v(-31.7, -40) * mm});
            skArc(sketch, "E197", {"start": v(-71.7, -40) * mm, "mid": v(-72.5, -39.2) * mm, "end": v(-73.3, -40) * mm});
            skArc(sketch, "E198", {"start": v(-73.3, -40) * mm, "mid": v(-72.5, -40.8) * mm, "end": v(-71.7, -40) * mm});
            skArc(sketch, "E199", {"start": v(-84.2, -32) * mm, "mid": v(-85, -31.2) * mm, "end": v(-85.8, -32) * mm});
            skArc(sketch, "E200", {"start": v(-85.8, -32) * mm, "mid": v(-85, -32.8) * mm, "end": v(-84.2, -32) * mm});
            skArc(sketch, "E201", {"start": v(28.3, 40) * mm, "mid": v(27.5, 40.8) * mm, "end": v(26.7, 40) * mm});
            skArc(sketch, "E202", {"start": v(26.7, 40) * mm, "mid": v(27.5, 39.2) * mm, "end": v(28.3, 40) * mm});
            skArc(sketch, "E203", {"start": v(8.3, 40) * mm, "mid": v(7.5, 40.8) * mm, "end": v(6.7, 40) * mm});
            skArc(sketch, "E204", {"start": v(6.7, 40) * mm, "mid": v(7.5, 39.2) * mm, "end": v(8.3, 40) * mm});
            skArc(sketch, "E205", {"start": v(-84.2, 27.5) * mm, "mid": v(-85, 28.3) * mm, "end": v(-85.8, 27.5) * mm});
            skArc(sketch, "E206", {"start": v(-85.8, 27.5) * mm, "mid": v(-85, 26.7) * mm, "end": v(-84.2, 27.5) * mm});
            skArc(sketch, "E207", {"start": v(-84.2, 1.2) * mm, "mid": v(-85, 2) * mm, "end": v(-85.8, 1.2) * mm});
            skArc(sketch, "E208", {"start": v(-85.8, 1.2) * mm, "mid": v(-85, 0.4) * mm, "end": v(-84.2, 1.2) * mm});
            skArc(sketch, "E209", {"start": v(-31.7, 40) * mm, "mid": v(-32.5, 40.8) * mm, "end": v(-33.3, 40) * mm});
            skArc(sketch, "E210", {"start": v(-33.3, 40) * mm, "mid": v(-32.5, 39.2) * mm, "end": v(-31.7, 40) * mm});
            skArc(sketch, "E211", {"start": v(-71.7, 40) * mm, "mid": v(-72.5, 40.8) * mm, "end": v(-73.3, 40) * mm});
            skArc(sketch, "E212", {"start": v(-73.3, 40) * mm, "mid": v(-72.5, 39.2) * mm, "end": v(-71.7, 40) * mm});
            skLineSegment(sketch, "E213", {"start": v(-76.47, -36.04) * mm, "end": v(-82.04, -30.47) * mm});
            skLineSegment(sketch, "E214", {"start": v(-82.5, -2.86) * mm, "end": v(-82.5, 27.94) * mm});
            skArc(sketch, "E215", {"start": v(-81.04, 31.47) * mm, "mid": v(-82.12, 29.85) * mm, "end": v(-82.5, 27.94) * mm});
            skLineSegment(sketch, "E216", {"start": v(87.5, 42.5) * mm, "end": v(87.5, -42.5) * mm});
            skLineSegment(sketch, "E217", {"start": v(-87.5, 42.5) * mm, "end": v(87.5, 42.5) * mm});
            skArc(sketch, "E218", {"start": v(-80.35, -37.5) * mm, "mid": v(-82.5, -35.35) * mm, "end": v(-84.65, -37.5) * mm});
            skArc(sketch, "E219", {"start": v(-84.65, -37.5) * mm, "mid": v(-82.5, -39.65) * mm, "end": v(-80.35, -37.5) * mm});
            skArc(sketch, "E220", {"start": v(19.65, -37.5) * mm, "mid": v(17.5, -35.35) * mm, "end": v(15.35, -37.5) * mm});
            skArc(sketch, "E221", {"start": v(15.35, -37.5) * mm, "mid": v(17.5, -39.65) * mm, "end": v(19.65, -37.5) * mm});
            skArc(sketch, "E222", {"start": v(-80.35, 37.5) * mm, "mid": v(-82.5, 39.65) * mm, "end": v(-84.65, 37.5) * mm});
            skArc(sketch, "E223", {"start": v(-84.65, 37.5) * mm, "mid": v(-82.5, 35.35) * mm, "end": v(-80.35, 37.5) * mm});
            skArc(sketch, "E224", {"start": v(84.65, 37.5) * mm, "mid": v(82.5, 39.65) * mm, "end": v(80.35, 37.5) * mm});
            skArc(sketch, "E225", {"start": v(80.35, 37.5) * mm, "mid": v(82.5, 35.35) * mm, "end": v(84.65, 37.5) * mm});
            skArc(sketch, "E226", {"start": v(84.65, -37.5) * mm, "mid": v(82.5, -35.35) * mm, "end": v(80.35, -37.5) * mm});
            skArc(sketch, "E227", {"start": v(80.35, -37.5) * mm, "mid": v(82.5, -39.65) * mm, "end": v(84.65, -37.5) * mm});
            skArc(sketch, "E228", {"start": v(19.65, 37.5) * mm, "mid": v(17.5, 39.65) * mm, "end": v(15.35, 37.5) * mm});
            skArc(sketch, "E229", {"start": v(15.35, 37.5) * mm, "mid": v(17.5, 35.35) * mm, "end": v(19.65, 37.5) * mm});
            skLineSegment(sketch, "E230", {"start": v(-72.53, 37.2) * mm, "end": v(-9.68, 37.19) * mm});
            skLineSegment(sketch, "E231", {"start": v(-9.68, 37.19) * mm, "end": v(-9.68, 36.75) * mm});
            skLineSegment(sketch, "E232", {"start": v(0.44, 36.75) * mm, "end": v(0.44, 37.19) * mm});
            skLineSegment(sketch, "E233", {"start": v(0.44, 37.19) * mm, "end": v(8.25, 37.2) * mm});
            skLineSegment(sketch, "E234", {"start": v(0.44, 17.65) * mm, "end": v(0.04, 17.65) * mm});
            skLineSegment(sketch, "E235", {"start": v(0.44, 12.03) * mm, "end": v(0.44, 17.65) * mm});
            skLineSegment(sketch, "E236", {"start": v(0.44, 17.65) * mm, "end": v(-0.04, 17.65) * mm});
            skLineSegment(sketch, "E237", {"start": v(-0.04, 17.65) * mm, "end": v(-0.04, 31.14) * mm});
            skLineSegment(sketch, "E238", {"start": v(-0.04, 31.14) * mm, "end": v(0.04, 31.14) * mm});
            skLineSegment(sketch, "E239", {"start": v(0.04, 31.14) * mm, "end": v(0.04, 31.13) * mm});
            skLineSegment(sketch, "E240", {"start": v(0.04, 31.13) * mm, "end": v(0.44, 31.13) * mm});
            skLineSegment(sketch, "E241", {"start": v(-9.68, 12.03) * mm, "end": v(0.44, 12.03) * mm});
            skLineSegment(sketch, "E242", {"start": v(-9.68, 17.65) * mm, "end": v(-9.68, 12.03) * mm});
            skLineSegment(sketch, "E243", {"start": v(-9.68, 17.65) * mm, "end": v(-9.28, 17.65) * mm});
            skLineSegment(sketch, "E244", {"start": v(-9.28, 17.65) * mm, "end": v(-9.19, 17.65) * mm});
            skLineSegment(sketch, "E245", {"start": v(-9.19, 17.65) * mm, "end": v(-9.19, 31.12) * mm});
            skLineSegment(sketch, "E246", {"start": v(-9.19, 31.12) * mm, "end": v(-9.68, 31.12) * mm});
            skLineSegment(sketch, "E247", {"start": v(-9.68, 31.12) * mm, "end": v(-9.68, 36.75) * mm});
            skLineSegment(sketch, "E248", {"start": v(-9.68, 31.12) * mm, "end": v(-9.28, 31.12) * mm});
            skLineSegment(sketch, "E249", {"start": v(0.44, 31.13) * mm, "end": v(0.44, 36.75) * mm});
            skArc(sketch, "E250", {"start": v(11.79, 35.73) * mm, "mid": v(10.17, 36.82) * mm, "end": v(8.25, 37.2) * mm});
            skArc(sketch, "E251", {"start": v(26.77, 37.2) * mm, "mid": v(24.86, 36.82) * mm, "end": v(23.24, 35.73) * mm});
            skArc(sketch, "E252", {"start": v(-72.53, 37.2) * mm, "mid": v(-74.45, 36.82) * mm, "end": v(-76.07, 35.73) * mm});
            skLineSegment(sketch, "E253", {"start": v(26.77, 37.2) * mm, "end": v(72.53, 37.2) * mm});
            skArc(sketch, "E254", {"start": v(76.07, 35.73) * mm, "mid": v(74.45, 36.82) * mm, "end": v(72.53, 37.2) * mm});
            skArc(sketch, "E255", {"start": v(13.98, 33.54) * mm, "mid": v(17.51, 32.08) * mm, "end": v(21.05, 33.54) * mm});
            skArc(sketch, "E256", {"start": v(-80.71, 31.09) * mm, "mid": v(-81.8, 29.46) * mm, "end": v(-82.18, 27.55) * mm});
            skArc(sketch, "E257", {"start": v(82.22, 27.5) * mm, "mid": v(81.84, 29.42) * mm, "end": v(80.76, 31.04) * mm});
            skLineSegment(sketch, "E258", {"start": v(11.79, 35.73) * mm, "end": v(13.98, 33.54) * mm});
            skLineSegment(sketch, "E259", {"start": v(21.05, 33.54) * mm, "end": v(23.24, 35.73) * mm});
            skLineSegment(sketch, "E260", {"start": v(-80.71, 31.09) * mm, "end": v(-76.07, 35.73) * mm});
            skLineSegment(sketch, "E261", {"start": v(80.76, 31.04) * mm, "end": v(76.07, 35.73) * mm});
            skArc(sketch, "E262", {"start": v(80.76, -31.04) * mm, "mid": v(81.84, -29.42) * mm, "end": v(82.22, -27.5) * mm});
            skArc(sketch, "E263", {"start": v(-82.18, -27.55) * mm, "mid": v(-81.8, -29.46) * mm, "end": v(-80.71, -31.09) * mm});
            skLineSegment(sketch, "E264", {"start": v(11.78, -35.74) * mm, "end": v(13.98, -33.54) * mm});
            skArc(sketch, "E265", {"start": v(8.25, -37.2) * mm, "mid": v(10.16, -36.82) * mm, "end": v(11.78, -35.74) * mm});
            skLineSegment(sketch, "E266", {"start": v(21.05, -33.54) * mm, "end": v(23.24, -35.74) * mm});
            skArc(sketch, "E267", {"start": v(23.24, -35.74) * mm, "mid": v(24.87, -36.82) * mm, "end": v(26.78, -37.2) * mm});
            skLineSegment(sketch, "E268", {"start": v(72.53, -37.2) * mm, "end": v(26.78, -37.2) * mm});
            skArc(sketch, "E269", {"start": v(72.53, -37.2) * mm, "mid": v(74.44, -36.82) * mm, "end": v(76.06, -35.74) * mm});
            skLineSegment(sketch, "E270", {"start": v(8.25, -37.2) * mm, "end": v(-72.53, -37.2) * mm});
            skArc(sketch, "E271", {"start": v(-76.06, -35.74) * mm, "mid": v(-74.44, -36.82) * mm, "end": v(-72.53, -37.2) * mm});
            skArc(sketch, "E272", {"start": v(21.05, -33.54) * mm, "mid": v(17.51, -32.08) * mm, "end": v(13.98, -33.54) * mm});
            skLineSegment(sketch, "E273", {"start": v(80.76, -31.04) * mm, "end": v(76.06, -35.74) * mm});
            skLineSegment(sketch, "E274", {"start": v(-80.71, -31.09) * mm, "end": v(-76.06, -35.74) * mm});
            skLineSegment(sketch, "E275", {"start": v(82.22, 27.5) * mm, "end": v(82.22, -27.5) * mm});
            skLineSegment(sketch, "E276", {"start": v(-82.18, -27.55) * mm, "end": v(-82.18, 27.55) * mm});
            skArc(sketch, "E277", {"start": v(78.46, 29.93) * mm, "mid": v(77.66, 30.73) * mm, "end": v(76.86, 29.93) * mm});
            skArc(sketch, "E278", {"start": v(76.86, 29.93) * mm, "mid": v(77.66, 29.13) * mm, "end": v(78.46, 29.93) * mm});
            skArc(sketch, "E279", {"start": v(80.43, 18.31) * mm, "mid": v(79.63, 19.11) * mm, "end": v(78.83, 18.31) * mm});
            skArc(sketch, "E280", {"start": v(78.83, 18.31) * mm, "mid": v(79.63, 17.51) * mm, "end": v(80.43, 18.31) * mm});
            skArc(sketch, "E281", {"start": v(67.16, 18.48) * mm, "mid": v(66.36, 19.28) * mm, "end": v(65.56, 18.48) * mm});
            skArc(sketch, "E282", {"start": v(65.56, 18.48) * mm, "mid": v(66.36, 17.68) * mm, "end": v(67.16, 18.48) * mm});
            skArc(sketch, "E283", {"start": v(67.22, 30.18) * mm, "mid": v(66.42, 30.98) * mm, "end": v(65.62, 30.18) * mm});
            skArc(sketch, "E284", {"start": v(65.62, 30.18) * mm, "mid": v(66.42, 29.38) * mm, "end": v(67.22, 30.18) * mm});
            skArc(sketch, "E285", {"start": v(46.84, 28.5) * mm, "mid": v(46.24, 29.1) * mm, "end": v(45.64, 28.5) * mm});
            skArc(sketch, "E286", {"start": v(45.64, 28.5) * mm, "mid": v(46.24, 27.9) * mm, "end": v(46.84, 28.5) * mm});
            skArc(sketch, "E287", {"start": v(46.84, 14) * mm, "mid": v(46.24, 14.6) * mm, "end": v(45.64, 14) * mm});
            skArc(sketch, "E288", {"start": v(45.64, 14) * mm, "mid": v(46.24, 13.4) * mm, "end": v(46.84, 14) * mm});
            skArc(sketch, "E289", {"start": v(61.34, 14) * mm, "mid": v(60.74, 14.6) * mm, "end": v(60.14, 14) * mm});
            skArc(sketch, "E290", {"start": v(60.14, 14) * mm, "mid": v(60.74, 13.4) * mm, "end": v(61.34, 14) * mm});
            skArc(sketch, "E291", {"start": v(85.8, 32) * mm, "mid": v(85, 32.8) * mm, "end": v(84.2, 32) * mm});
            skArc(sketch, "E292", {"start": v(84.2, 32) * mm, "mid": v(85, 31.2) * mm, "end": v(85.8, 32) * mm});
            skArc(sketch, "E293", {"start": v(85.8, 2.25) * mm, "mid": v(85, 3.05) * mm, "end": v(84.2, 2.25) * mm});
            skArc(sketch, "E294", {"start": v(84.2, 2.25) * mm, "mid": v(85, 1.45) * mm, "end": v(85.8, 2.25) * mm});
            skSolve(sketch);
        }
        {
            var Q0;
            Q0=sQuery(id+"F0.wireOp",VERTEX,"E24.center");
            var Q1;
            Q1=sQuery(id+"F0.wireOp",VERTEX,"E22.center");
            var Q2;
            Q2=sQuery(id+"F0.wireOp",VERTEX,"E28.center");
            var Q3;
            Q3=sQuery(id+"F0.wireOp",VERTEX,"E16.center");
            var Q4;
            Q4=sQuery(id+"F0.wireOp",VERTEX,"E21.center");
            var Q5;
            Q5=sQuery(id+"F0.wireOp",VERTEX,"E18.center");
            var Q6;
            Q6=sQuery(id+"F0.wireOp",VERTEX,"E40.center");
            var Q7;
            Q7=sQuery(id+"F0.wireOp",VERTEX,"E38.center");
            var Q8;
            Q8=sQuery(id+"F0.wireOp",VERTEX,"E30.center");
            var Q9;
            Q9=sQuery(id+"F0.wireOp",VERTEX,"E33.center");
            var Q10;
            Q10=sQuery(id+"F0.wireOp",VERTEX,"E34.center");
            var Q11;
            Q11=sQuery(id+"F0.wireOp",VERTEX,"E37.center");
            var Q12;
            Q12=sQuery(id+"F0.wireOp",VERTEX,"E46.center");
            var Q13;
            Q13=sQuery(id+"F3.wireOp",VERTEX,"E291.center");
            var Q14;
            Q14=sQuery(id+"F3.wireOp",VERTEX,"E294.center");
            var Q15;
            Q15=sQuery(id+"F3.wireOp",VERTEX,"E208.center");
            var Q16;
            Q16=sQuery(id+"F3.wireOp",VERTEX,"E144.center");
            var Q17;
            Q17=sQuery(id+"F3.wireOp",VERTEX,"E96.center");
            var Q18;
            Q18=makeQuery(id+"F1.opExtrude","SWEPT_BODY",BODY,{"disambiguationData":[OSD([sQuery(id+"F0.wireOp",EDGE,"E3"),sQuery(id+"F0.wireOp",EDGE,"E0"),sQuery(id+"F0.wireOp",EDGE,"E1"),sQuery(id+"F0.wireOp",EDGE,"E2")])]});
            hole(context, id + "F4", {"style" : HoleStyle.C_SINK, "endStyle" : HoleEndStyle.THROUGH, "holeDiameter" : 2.3 * mm, "cSinkDiameter" : 4.5 * mm, "cSinkAngle" : 90 * degree, "majorDiameter" : 5 * mm, "startFromSketch" : true, "locations" : qUnion([Q0, Q1, Q2, Q3, Q4, Q5, Q6, Q7, Q8, Q9, Q10, Q11, Q12, Q13, Q14, Q15, Q16, Q17]), "scope" : qUnion([Q18]), "tappedDepth" : 12 * mm, "tapClearance" : 3});
        }
    });
